AUTODESK INVENTOR PART (.ipt)
format: ipt  version: 2021 (Build 250183000, 183)  size: 96,768 bytes
history: native  units: mm
features: extrude x1, fillet x1, sketch x1
ambient origin geometry x8: Origin, YZ Plane, XZ Plane, XY Plane, X Axis, Y Axis, Z Axis, Center Point
bodies: Body1 (feature_tree)
feature tree (3):
  extrude  "Extrusion17"  Depth=40.0mm
  fillet  "Fillet7"  Radius=8.0mm
  sketch  "Sketch18"  dims[d163=32.0mm d164=40.0mm d165=8.0mm d166=0.0mm d167=0.4mm]
